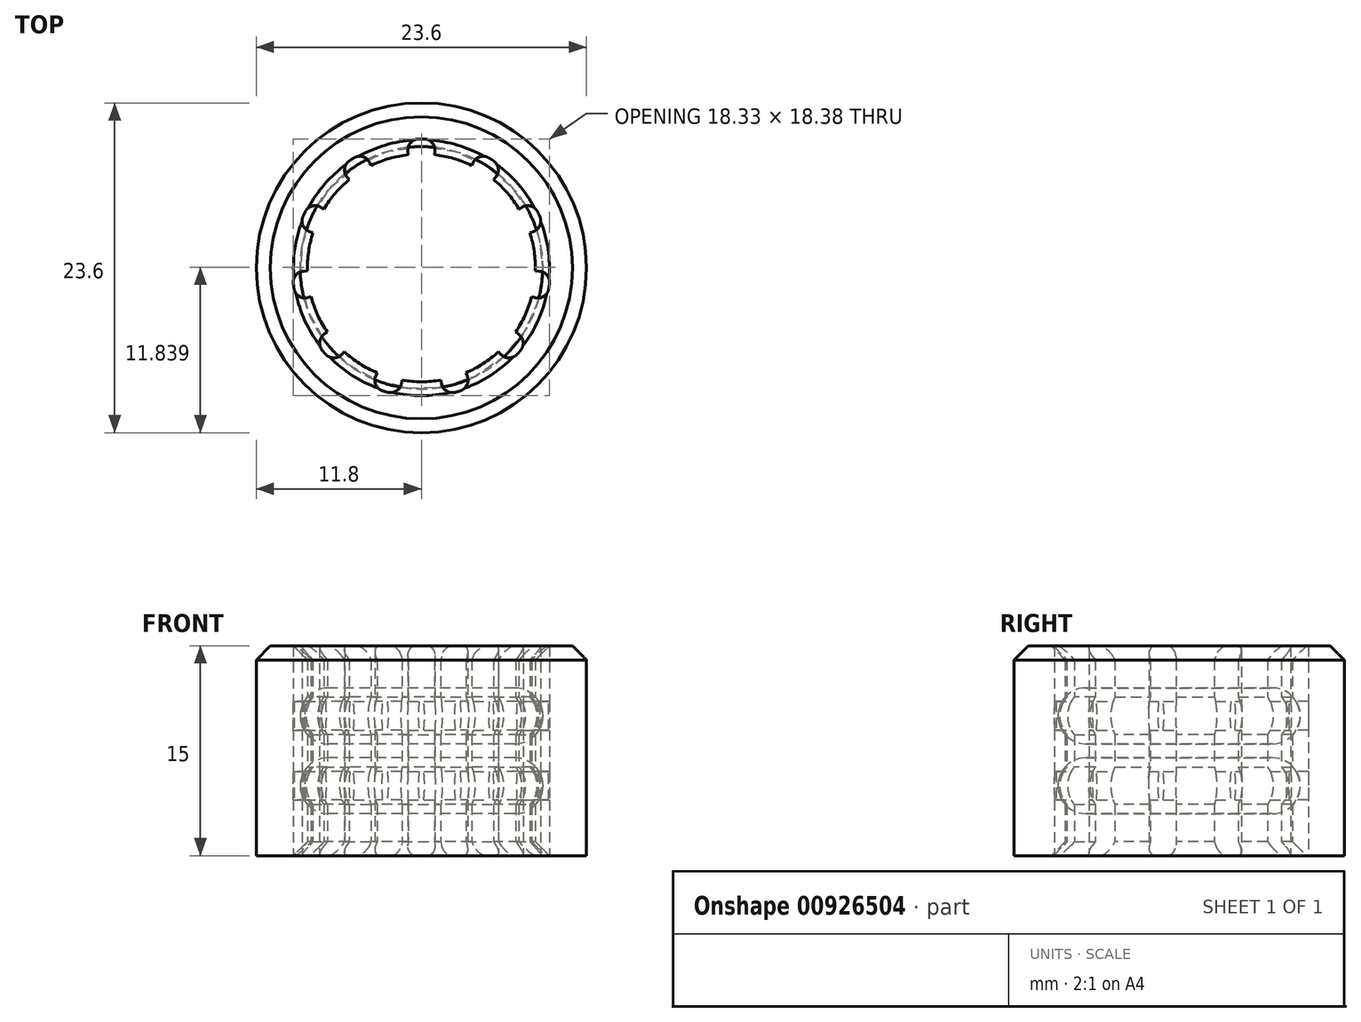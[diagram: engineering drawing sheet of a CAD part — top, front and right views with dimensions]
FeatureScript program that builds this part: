
annotation { "Feature Type Name" : "Feature", "Feature Type Description" : "" }
export const myFeature = defineFeature(function(context is Context, id is Id, definition is map)
    precondition{}
    {
        {
            var Q0;
            Q0=qCreatedBy(makeId("Top.planeOp"),FACE);
            var sketch = newSketch(context, id + "F0", { "sketchPlane" : qUnion([Q0])});
            skArc(sketch, "E0", {"start": v(-0.93, 8.1) * mm, "mid": v(-2.3, 7.82) * mm, "end": v(-3.6, 7.31) * mm});
            skCircle(sketch, "E1", {"center": v(0, 0) * mm, "radius": 11.8 * mm});
            skLineSegment(sketch, "E2", {"start": v(-0.93, 8.1) * mm, "end": v(-1.05, 9.17) * mm});
            skLineSegment(sketch, "E3.MirrorCS", {"start": v(0.93, 8.1) * mm, "end": v(1.05, 9.17) * mm});
            skArc(sketch, "E4", {"start": v(1.05, 9.17) * mm, "mid": v(0, 9.23) * mm, "end": v(-1.05, 9.17) * mm});
            skLineSegment(sketch, "E5.1.0", {"start": v(-5.16, 6.3) * mm, "end": v(-5.84, 7.14) * mm});
            skArc(sketch, "E5.1.1", {"start": v(-4.07, 8.28) * mm, "mid": v(-4.99, 7.76) * mm, "end": v(-5.84, 7.14) * mm});
            skLineSegment(sketch, "E5.1.2", {"start": v(-3.6, 7.31) * mm, "end": v(-4.07, 8.28) * mm});
            skLineSegment(sketch, "E5.2.0", {"start": v(-7.75, 2.52) * mm, "end": v(-8.78, 2.85) * mm});
            skArc(sketch, "E5.2.1", {"start": v(-7.9, 4.77) * mm, "mid": v(-8.4, 3.83) * mm, "end": v(-8.78, 2.85) * mm});
            skLineSegment(sketch, "E5.2.2", {"start": v(-6.98, 4.21) * mm, "end": v(-7.9, 4.77) * mm});
            skLineSegment(sketch, "E5.3.0", {"start": v(-7.88, -2.07) * mm, "end": v(-8.92, -2.35) * mm});
            skArc(sketch, "E5.3.1", {"start": v(-9.22, -0.26) * mm, "mid": v(-9.13, -1.31) * mm, "end": v(-8.92, -2.35) * mm});
            skLineSegment(sketch, "E5.3.2", {"start": v(-8.15, -0.23) * mm, "end": v(-9.22, -0.26) * mm});
            skLineSegment(sketch, "E5.4.0", {"start": v(-5.5, -6) * mm, "end": v(-6.24, -6.8) * mm});
            skArc(sketch, "E5.4.1", {"start": v(-7.62, -5.2) * mm, "mid": v(-6.97, -6.04) * mm, "end": v(-6.24, -6.8) * mm});
            skLineSegment(sketch, "E5.4.2", {"start": v(-6.73, -4.6) * mm, "end": v(-7.62, -5.2) * mm});
            skLineSegment(sketch, "E5.5.0", {"start": v(-1.39, -8.03) * mm, "end": v(-1.57, -9.1) * mm});
            skArc(sketch, "E5.5.1", {"start": v(-3.6, -8.5) * mm, "mid": v(-2.6, -8.85) * mm, "end": v(-1.57, -9.1) * mm});
            skLineSegment(sketch, "E5.5.2", {"start": v(-3.17, -7.5) * mm, "end": v(-3.6, -8.5) * mm});
            skLineSegment(sketch, "E5.6.0", {"start": v(3.17, -7.5) * mm, "end": v(3.6, -8.5) * mm});
            skArc(sketch, "E5.6.1", {"start": v(1.57, -9.1) * mm, "mid": v(2.6, -8.85) * mm, "end": v(3.6, -8.5) * mm});
            skLineSegment(sketch, "E5.6.2", {"start": v(1.39, -8.03) * mm, "end": v(1.57, -9.1) * mm});
            skLineSegment(sketch, "E5.7.0", {"start": v(6.73, -4.6) * mm, "end": v(7.62, -5.2) * mm});
            skArc(sketch, "E5.7.1", {"start": v(6.24, -6.8) * mm, "mid": v(6.97, -6.04) * mm, "end": v(7.62, -5.2) * mm});
            skLineSegment(sketch, "E5.7.2", {"start": v(5.5, -6) * mm, "end": v(6.24, -6.8) * mm});
            skLineSegment(sketch, "E5.8.0", {"start": v(8.15, -0.23) * mm, "end": v(9.22, -0.26) * mm});
            skArc(sketch, "E5.8.1", {"start": v(8.92, -2.35) * mm, "mid": v(9.13, -1.31) * mm, "end": v(9.22, -0.26) * mm});
            skLineSegment(sketch, "E5.8.2", {"start": v(7.88, -2.07) * mm, "end": v(8.92, -2.35) * mm});
            skArc(sketch, "E6.trimOffspring", {"start": v(-5.16, 6.3) * mm, "mid": v(-6.16, 5.34) * mm, "end": v(-6.98, 4.21) * mm});
            skArc(sketch, "E7.trimOffspring", {"start": v(-7.75, 2.52) * mm, "mid": v(-8.07, 1.16) * mm, "end": v(-8.15, -0.23) * mm});
            skArc(sketch, "E8.trimOffspring", {"start": v(-7.88, -2.07) * mm, "mid": v(-7.41, -3.39) * mm, "end": v(-6.73, -4.6) * mm});
            skArc(sketch, "E9.trimOffspring", {"start": v(-5.5, -6) * mm, "mid": v(-4.4, -6.86) * mm, "end": v(-3.17, -7.5) * mm});
            skArc(sketch, "E10.trimOffspring", {"start": v(-1.39, -8.03) * mm, "mid": v(0, -8.15) * mm, "end": v(1.39, -8.03) * mm});
            skArc(sketch, "E11.trimOffspring", {"start": v(3.17, -7.5) * mm, "mid": v(4.4, -6.86) * mm, "end": v(5.5, -6) * mm});
            skArc(sketch, "E12.trimOffspring", {"start": v(6.73, -4.6) * mm, "mid": v(8.07, 1.16) * mm, "end": v(5.16, 6.3) * mm});
            skArc(sketch, "E13.trimOffspring", {"start": v(3.6, 7.31) * mm, "mid": v(2.3, 7.82) * mm, "end": v(0.93, 8.1) * mm});
            skLineSegment(sketch, "E14.1.9.0", {"start": v(6.98, 4.21) * mm, "end": v(7.9, 4.77) * mm});
            skArc(sketch, "E14.3.9.0", {"start": v(8.78, 2.85) * mm, "mid": v(8.4, 3.83) * mm, "end": v(7.9, 4.77) * mm});
            skLineSegment(sketch, "E14.7.9.0", {"start": v(7.75, 2.52) * mm, "end": v(8.78, 2.85) * mm});
            skLineSegment(sketch, "E15.1.10.0", {"start": v(3.6, 7.31) * mm, "end": v(4.07, 8.28) * mm});
            skArc(sketch, "E15.3.10.0", {"start": v(5.84, 7.14) * mm, "mid": v(4.99, 7.76) * mm, "end": v(4.07, 8.28) * mm});
            skLineSegment(sketch, "E15.7.10.0", {"start": v(5.16, 6.3) * mm, "end": v(5.84, 7.14) * mm});
            skSolve(sketch);
        }
        {
            var Q0;
            Q0=makeQuery(id+"F0.imprint","IMPRINT",FACE,{"disambiguationData":[TD([[makeQuery(id+"F0.imprint","IMPRINT",EDGE,{"derivedFrom":sQuery(id+"F0.wireOp",EDGE,"E0")}),-1.0]])]});
            extrude(context, id + "F1", {"entities" : qUnion([Q0]), "depth" : 15 * mm, "offsetDistance" : 25 * mm});
        }
        {
            var Q0;
            Q0=makeQuery(id+"F1.opExtrude","CAP_EDGE",EDGE,{"disambiguationData":[OSD([sQuery(id+"F0.wireOp",EDGE,"E13.trimOffspring")])],"isStart":false});
            var Q1;
            {var subQ0=sQuery(id+"F0.wireOp",EDGE,"E12.trimOffspring");Q1=makeQuery(id+"F1.opExtrude","CAP_EDGE",EDGE,{"disambiguationData":[OSD([subQ0]),TDD([makeQuery(id+"F0.imprint","IMPRINT",EDGE,{"disambiguationData":[TD([[makeQuery(id+"F0.imprint","INTERSECT",VERTEX,{"derivedFrom":[subQ0,sQuery(id+"F0.wireOp",EDGE,"E15.7.10.0")]}),1.0]])],"derivedFrom":subQ0})])],"isStart":false});}
            var Q2;
            {var subQ0=sQuery(id+"F0.wireOp",EDGE,"E12.trimOffspring");Q2=makeQuery(id+"F1.opExtrude","CAP_EDGE",EDGE,{"disambiguationData":[OSD([subQ0]),TDD([makeQuery(id+"F0.imprint","IMPRINT",EDGE,{"disambiguationData":[TD([[makeQuery(id+"F0.imprint","INTERSECT",VERTEX,{"derivedFrom":[sQuery(id+"F0.wireOp",EDGE,"E5.8.0"),subQ0]}),-1.0]])],"derivedFrom":subQ0})])],"isStart":false});}
            var Q3;
            {var subQ0=sQuery(id+"F0.wireOp",EDGE,"E12.trimOffspring");Q3=makeQuery(id+"F1.opExtrude","CAP_EDGE",EDGE,{"disambiguationData":[OSD([subQ0]),TDD([makeQuery(id+"F0.imprint","IMPRINT",EDGE,{"disambiguationData":[TD([[makeQuery(id+"F0.imprint","INTERSECT",VERTEX,{"derivedFrom":[sQuery(id+"F0.wireOp",EDGE,"E5.7.0"),subQ0]}),-1.0]])],"derivedFrom":subQ0})])],"isStart":false});}
            var Q4;
            Q4=makeQuery(id+"F1.opExtrude","CAP_EDGE",EDGE,{"disambiguationData":[OSD([sQuery(id+"F0.wireOp",EDGE,"E11.trimOffspring")])],"isStart":false});
            var Q5;
            Q5=makeQuery(id+"F1.opExtrude","CAP_EDGE",EDGE,{"disambiguationData":[OSD([sQuery(id+"F0.wireOp",EDGE,"E10.trimOffspring")])],"isStart":false});
            var Q6;
            Q6=makeQuery(id+"F1.opExtrude","CAP_EDGE",EDGE,{"disambiguationData":[OSD([sQuery(id+"F0.wireOp",EDGE,"E9.trimOffspring")])],"isStart":false});
            var Q7;
            Q7=makeQuery(id+"F1.opExtrude","CAP_EDGE",EDGE,{"disambiguationData":[OSD([sQuery(id+"F0.wireOp",EDGE,"E8.trimOffspring")])],"isStart":false});
            var Q8;
            Q8=makeQuery(id+"F1.opExtrude","CAP_EDGE",EDGE,{"disambiguationData":[OSD([sQuery(id+"F0.wireOp",EDGE,"E7.trimOffspring")])],"isStart":false});
            var Q9;
            Q9=makeQuery(id+"F1.opExtrude","CAP_EDGE",EDGE,{"disambiguationData":[OSD([sQuery(id+"F0.wireOp",EDGE,"E6.trimOffspring")])],"isStart":false});
            var Q10;
            Q10=makeQuery(id+"F1.opExtrude","CAP_EDGE",EDGE,{"disambiguationData":[OSD([sQuery(id+"F0.wireOp",EDGE,"E0")])],"isStart":false});
            var Q11;
            Q11=makeQuery(id+"F1.opExtrude","CAP_EDGE",EDGE,{"disambiguationData":[OSD([sQuery(id+"F0.wireOp",EDGE,"E6.trimOffspring")])],"isStart":true});
            var Q12;
            Q12=makeQuery(id+"F1.opExtrude","CAP_EDGE",EDGE,{"disambiguationData":[OSD([sQuery(id+"F0.wireOp",EDGE,"E7.trimOffspring")])],"isStart":true});
            var Q13;
            Q13=makeQuery(id+"F1.opExtrude","CAP_EDGE",EDGE,{"disambiguationData":[OSD([sQuery(id+"F0.wireOp",EDGE,"E8.trimOffspring")])],"isStart":true});
            var Q14;
            Q14=makeQuery(id+"F1.opExtrude","CAP_EDGE",EDGE,{"disambiguationData":[OSD([sQuery(id+"F0.wireOp",EDGE,"E9.trimOffspring")])],"isStart":true});
            var Q15;
            Q15=makeQuery(id+"F1.opExtrude","CAP_EDGE",EDGE,{"disambiguationData":[OSD([sQuery(id+"F0.wireOp",EDGE,"E10.trimOffspring")])],"isStart":true});
            var Q16;
            Q16=makeQuery(id+"F1.opExtrude","CAP_EDGE",EDGE,{"disambiguationData":[OSD([sQuery(id+"F0.wireOp",EDGE,"E11.trimOffspring")])],"isStart":true});
            var Q17;
            {var subQ0=sQuery(id+"F0.wireOp",EDGE,"E12.trimOffspring");Q17=makeQuery(id+"F1.opExtrude","CAP_EDGE",EDGE,{"disambiguationData":[OSD([subQ0]),TDD([makeQuery(id+"F0.imprint","IMPRINT",EDGE,{"disambiguationData":[TD([[makeQuery(id+"F0.imprint","INTERSECT",VERTEX,{"derivedFrom":[sQuery(id+"F0.wireOp",EDGE,"E5.7.0"),subQ0]}),-1.0]])],"derivedFrom":subQ0})])],"isStart":true});}
            var Q18;
            {var subQ0=sQuery(id+"F0.wireOp",EDGE,"E12.trimOffspring");Q18=makeQuery(id+"F1.opExtrude","CAP_EDGE",EDGE,{"disambiguationData":[OSD([subQ0]),TDD([makeQuery(id+"F0.imprint","IMPRINT",EDGE,{"disambiguationData":[TD([[makeQuery(id+"F0.imprint","INTERSECT",VERTEX,{"derivedFrom":[sQuery(id+"F0.wireOp",EDGE,"E5.8.0"),subQ0]}),-1.0]])],"derivedFrom":subQ0})])],"isStart":true});}
            var Q19;
            {var subQ0=sQuery(id+"F0.wireOp",EDGE,"E12.trimOffspring");Q19=makeQuery(id+"F1.opExtrude","CAP_EDGE",EDGE,{"disambiguationData":[OSD([subQ0]),TDD([makeQuery(id+"F0.imprint","IMPRINT",EDGE,{"disambiguationData":[TD([[makeQuery(id+"F0.imprint","INTERSECT",VERTEX,{"derivedFrom":[subQ0,sQuery(id+"F0.wireOp",EDGE,"E15.7.10.0")]}),1.0]])],"derivedFrom":subQ0})])],"isStart":true});}
            var Q20;
            Q20=makeQuery(id+"F1.opExtrude","CAP_EDGE",EDGE,{"disambiguationData":[OSD([sQuery(id+"F0.wireOp",EDGE,"E13.trimOffspring")])],"isStart":true});
            var Q21;
            Q21=makeQuery(id+"F1.opExtrude","CAP_EDGE",EDGE,{"disambiguationData":[OSD([sQuery(id+"F0.wireOp",EDGE,"E0")])],"isStart":true});
            chamfer(context, id + "F2", {"entities" : qUnion([Q0, Q1, Q2, Q3, Q4, Q5, Q6, Q7, Q8, Q9, Q10, Q11, Q12, Q13, Q14, Q15, Q16, Q17, Q18, Q19, Q20, Q21]), "width" : 1 * mm, "tangentPropagation" : true});
        }
        {
            var Q0;
            Q0=qCreatedBy(makeId("Top.planeOp"),FACE);
            cPlane(context, id + "F3", {"entities" : qUnion([Q0]), "cplaneType" : CPlaneType.OFFSET, "offset" : 5 * mm, "width" : 150 * mm, "height" : 150 * mm});
        }
        {
            var Q0;
            Q0=qCreatedBy(id+"F3.planeOp",FACE);
            var sketch = newSketch(context, id + "F4", { "sketchPlane" : qUnion([Q0])});
            skCircle(sketch, "E16", {"center": v(0, 0) * mm, "radius": 8.67 * mm});
            skSolve(sketch);
        }
        {
            var Q0;
            Q0=makeQuery(id+"F4.imprint","IMPRINT",FACE,{"disambiguationData":[TD([[makeQuery(id+"F4.imprint","IMPRINT",EDGE,{"derivedFrom":sQuery(id+"F4.wireOp",EDGE,"E16")}),1.0]])]});
            extrude(context, id + "F5", {"entities" : qUnion([Q0]), "depth" : 2 * mm, "offsetDistance" : 25 * mm, "hasSecondDirection" : true, "secondDirectionOppositeDirection" : true, "secondDirectionDepth" : 2 * mm});
        }
        {
            var Q0;
            Q0=makeQuery(id+"F5.opExtrude","SWEPT_FACE",FACE,{"disambiguationData":[OSD([sQuery(id+"F4.wireOp",EDGE,"E16")])]});
            fillet(context, id + "F6", {"entities" : qUnion([Q0]), "radius" : 2 * mm, "tangentPropagation" : true, "allowEdgeOverflow" : false});
        }
        {
            var Q0;
            Q0=makeQuery(id+"F5.opExtrude","SWEPT_BODY",BODY,{"disambiguationData":[OSD([sQuery(id+"F4.wireOp",EDGE,"E16")])]});
            var Q1;
            Q1=makeQuery(id+"F1.opExtrude","SWEPT_BODY",BODY,{"disambiguationData":[OSD([sQuery(id+"F0.wireOp",EDGE,"E0"),sQuery(id+"F0.wireOp",EDGE,"E1"),sQuery(id+"F0.wireOp",EDGE,"E2"),sQuery(id+"F0.wireOp",EDGE,"E3.MirrorCS"),sQuery(id+"F0.wireOp",EDGE,"E4"),sQuery(id+"F0.wireOp",EDGE,"E5.1.0"),sQuery(id+"F0.wireOp",EDGE,"E5.1.1"),sQuery(id+"F0.wireOp",EDGE,"E5.1.2"),sQuery(id+"F0.wireOp",EDGE,"E5.2.0"),sQuery(id+"F0.wireOp",EDGE,"E5.2.1"),sQuery(id+"F0.wireOp",EDGE,"E5.2.2"),sQuery(id+"F0.wireOp",EDGE,"E5.3.0"),sQuery(id+"F0.wireOp",EDGE,"E5.3.1"),sQuery(id+"F0.wireOp",EDGE,"E5.3.2"),sQuery(id+"F0.wireOp",EDGE,"E5.4.0"),sQuery(id+"F0.wireOp",EDGE,"E5.4.1"),sQuery(id+"F0.wireOp",EDGE,"E5.4.2"),sQuery(id+"F0.wireOp",EDGE,"E5.5.0"),sQuery(id+"F0.wireOp",EDGE,"E5.5.1"),sQuery(id+"F0.wireOp",EDGE,"E5.5.2"),sQuery(id+"F0.wireOp",EDGE,"E5.6.0"),sQuery(id+"F0.wireOp",EDGE,"E5.6.1"),sQuery(id+"F0.wireOp",EDGE,"E5.6.2"),sQuery(id+"F0.wireOp",EDGE,"E5.7.0"),sQuery(id+"F0.wireOp",EDGE,"E5.7.1"),sQuery(id+"F0.wireOp",EDGE,"E5.7.2"),sQuery(id+"F0.wireOp",EDGE,"E5.8.0"),sQuery(id+"F0.wireOp",EDGE,"E5.8.1"),sQuery(id+"F0.wireOp",EDGE,"E5.8.2"),sQuery(id+"F0.wireOp",EDGE,"E6.trimOffspring"),sQuery(id+"F0.wireOp",EDGE,"E7.trimOffspring"),sQuery(id+"F0.wireOp",EDGE,"E8.trimOffspring"),sQuery(id+"F0.wireOp",EDGE,"E9.trimOffspring"),sQuery(id+"F0.wireOp",EDGE,"E10.trimOffspring"),sQuery(id+"F0.wireOp",EDGE,"E11.trimOffspring"),sQuery(id+"F0.wireOp",EDGE,"E12.trimOffspring"),sQuery(id+"F0.wireOp",EDGE,"E13.trimOffspring"),sQuery(id+"F0.wireOp",EDGE,"E14.1.9.0"),sQuery(id+"F0.wireOp",EDGE,"E14.3.9.0"),sQuery(id+"F0.wireOp",EDGE,"E14.7.9.0"),sQuery(id+"F0.wireOp",EDGE,"E15.1.10.0"),sQuery(id+"F0.wireOp",EDGE,"E15.3.10.0"),sQuery(id+"F0.wireOp",EDGE,"E15.7.10.0")])]});
            booleanBodies(context, id + "F7", {"operationType" : BooleanOperationType.SUBTRACTION, "tools" : qUnion([Q0]), "targets" : qUnion([Q1]), "keepTools" : true});
        }
        {
            var Q0;
            Q0=makeQuery(id+"F1.opExtrude","CAP_EDGE",EDGE,{"disambiguationData":[OSD([sQuery(id+"F0.wireOp",EDGE,"E1")])],"isStart":false});
            chamfer(context, id + "F8", {"entities" : qUnion([Q0]), "width" : 1 * mm, "tangentPropagation" : true});
        }
        {
            var Q0;
            Q0=makeQuery(id+"F5.opExtrude","SWEPT_BODY",BODY,{"disambiguationData":[OSD([sQuery(id+"F4.wireOp",EDGE,"E16")])]});
            transform(context, id + "F9", {"entities" : qUnion([Q0]), "transformType" : TransformType.TRANSLATION_3D, "dx" : 0 * mm, "dy" : 0 * mm, "dz" : 5 * mm, "makeCopy" : true});
        }
        {
            var Q0;
            Q0=makeQuery(id+"F9.opPattern","COPY",BODY,{"derivedFrom":makeQuery(id+"F5.opExtrude","SWEPT_BODY",BODY,{"disambiguationData":[OSD([sQuery(id+"F4.wireOp",EDGE,"E16")])]}),"instanceName":"1"});
            var Q1;
            Q1=makeQuery(id+"F1.opExtrude","SWEPT_BODY",BODY,{"disambiguationData":[OSD([sQuery(id+"F0.wireOp",EDGE,"E0"),sQuery(id+"F0.wireOp",EDGE,"E1"),sQuery(id+"F0.wireOp",EDGE,"E2"),sQuery(id+"F0.wireOp",EDGE,"E3.MirrorCS"),sQuery(id+"F0.wireOp",EDGE,"E4"),sQuery(id+"F0.wireOp",EDGE,"E5.1.0"),sQuery(id+"F0.wireOp",EDGE,"E5.1.1"),sQuery(id+"F0.wireOp",EDGE,"E5.1.2"),sQuery(id+"F0.wireOp",EDGE,"E5.2.0"),sQuery(id+"F0.wireOp",EDGE,"E5.2.1"),sQuery(id+"F0.wireOp",EDGE,"E5.2.2"),sQuery(id+"F0.wireOp",EDGE,"E5.3.0"),sQuery(id+"F0.wireOp",EDGE,"E5.3.1"),sQuery(id+"F0.wireOp",EDGE,"E5.3.2"),sQuery(id+"F0.wireOp",EDGE,"E5.4.0"),sQuery(id+"F0.wireOp",EDGE,"E5.4.1"),sQuery(id+"F0.wireOp",EDGE,"E5.4.2"),sQuery(id+"F0.wireOp",EDGE,"E5.5.0"),sQuery(id+"F0.wireOp",EDGE,"E5.5.1"),sQuery(id+"F0.wireOp",EDGE,"E5.5.2"),sQuery(id+"F0.wireOp",EDGE,"E5.6.0"),sQuery(id+"F0.wireOp",EDGE,"E5.6.1"),sQuery(id+"F0.wireOp",EDGE,"E5.6.2"),sQuery(id+"F0.wireOp",EDGE,"E5.7.0"),sQuery(id+"F0.wireOp",EDGE,"E5.7.1"),sQuery(id+"F0.wireOp",EDGE,"E5.7.2"),sQuery(id+"F0.wireOp",EDGE,"E5.8.0"),sQuery(id+"F0.wireOp",EDGE,"E5.8.1"),sQuery(id+"F0.wireOp",EDGE,"E5.8.2"),sQuery(id+"F0.wireOp",EDGE,"E6.trimOffspring"),sQuery(id+"F0.wireOp",EDGE,"E7.trimOffspring"),sQuery(id+"F0.wireOp",EDGE,"E8.trimOffspring"),sQuery(id+"F0.wireOp",EDGE,"E9.trimOffspring"),sQuery(id+"F0.wireOp",EDGE,"E10.trimOffspring"),sQuery(id+"F0.wireOp",EDGE,"E11.trimOffspring"),sQuery(id+"F0.wireOp",EDGE,"E12.trimOffspring"),sQuery(id+"F0.wireOp",EDGE,"E13.trimOffspring"),sQuery(id+"F0.wireOp",EDGE,"E14.1.9.0"),sQuery(id+"F0.wireOp",EDGE,"E14.3.9.0"),sQuery(id+"F0.wireOp",EDGE,"E14.7.9.0"),sQuery(id+"F0.wireOp",EDGE,"E15.1.10.0"),sQuery(id+"F0.wireOp",EDGE,"E15.3.10.0"),sQuery(id+"F0.wireOp",EDGE,"E15.7.10.0")])]});
            booleanBodies(context, id + "F10", {"operationType" : BooleanOperationType.SUBTRACTION, "tools" : qUnion([Q0]), "targets" : qUnion([Q1]), "keepTools" : true});
        }
        {
            var Q0;
            Q0=makeQuery(id+"F1.opExtrude","SWEPT_EDGE",EDGE,{"disambiguationData":[OSD([sQuery(id+"F0.wireOp",EDGE,"E5.1.1"),sQuery(id+"F0.wireOp",EDGE,"E5.1.2")])]});
            var Q1;
            Q1=makeQuery(id+"F1.opExtrude","SWEPT_EDGE",EDGE,{"disambiguationData":[OSD([sQuery(id+"F0.wireOp",EDGE,"E2"),sQuery(id+"F0.wireOp",EDGE,"E4")])]});
            var Q2;
            Q2=makeQuery(id+"F1.opExtrude","SWEPT_EDGE",EDGE,{"disambiguationData":[OSD([sQuery(id+"F0.wireOp",EDGE,"E15.1.10.0"),sQuery(id+"F0.wireOp",EDGE,"E15.3.10.0")])]});
            var Q3;
            Q3=makeQuery(id+"F1.opExtrude","SWEPT_EDGE",EDGE,{"disambiguationData":[OSD([sQuery(id+"F0.wireOp",EDGE,"E3.MirrorCS"),sQuery(id+"F0.wireOp",EDGE,"E4")])]});
            var Q4;
            Q4=makeQuery(id+"F1.opExtrude","SWEPT_EDGE",EDGE,{"disambiguationData":[OSD([sQuery(id+"F0.wireOp",EDGE,"E15.3.10.0"),sQuery(id+"F0.wireOp",EDGE,"E15.7.10.0")])]});
            var Q5;
            Q5=makeQuery(id+"F1.opExtrude","SWEPT_EDGE",EDGE,{"disambiguationData":[OSD([sQuery(id+"F0.wireOp",EDGE,"E14.1.9.0"),sQuery(id+"F0.wireOp",EDGE,"E14.3.9.0")])]});
            var Q6;
            Q6=makeQuery(id+"F1.opExtrude","SWEPT_EDGE",EDGE,{"disambiguationData":[OSD([sQuery(id+"F0.wireOp",EDGE,"E5.8.0"),sQuery(id+"F0.wireOp",EDGE,"E5.8.1")])]});
            var Q7;
            Q7=makeQuery(id+"F1.opExtrude","SWEPT_EDGE",EDGE,{"disambiguationData":[OSD([sQuery(id+"F0.wireOp",EDGE,"E5.7.0"),sQuery(id+"F0.wireOp",EDGE,"E5.7.1")])]});
            var Q8;
            Q8=makeQuery(id+"F1.opExtrude","SWEPT_EDGE",EDGE,{"disambiguationData":[OSD([sQuery(id+"F0.wireOp",EDGE,"E14.3.9.0"),sQuery(id+"F0.wireOp",EDGE,"E14.7.9.0")])]});
            var Q9;
            Q9=makeQuery(id+"F1.opExtrude","SWEPT_EDGE",EDGE,{"disambiguationData":[OSD([sQuery(id+"F0.wireOp",EDGE,"E5.8.1"),sQuery(id+"F0.wireOp",EDGE,"E5.8.2")])]});
            var Q10;
            Q10=makeQuery(id+"F1.opExtrude","SWEPT_EDGE",EDGE,{"disambiguationData":[OSD([sQuery(id+"F0.wireOp",EDGE,"E5.7.1"),sQuery(id+"F0.wireOp",EDGE,"E5.7.2")])]});
            var Q11;
            Q11=makeQuery(id+"F1.opExtrude","SWEPT_EDGE",EDGE,{"disambiguationData":[OSD([sQuery(id+"F0.wireOp",EDGE,"E5.6.0"),sQuery(id+"F0.wireOp",EDGE,"E5.6.1")])]});
            var Q12;
            Q12=makeQuery(id+"F1.opExtrude","SWEPT_EDGE",EDGE,{"disambiguationData":[OSD([sQuery(id+"F0.wireOp",EDGE,"E5.6.1"),sQuery(id+"F0.wireOp",EDGE,"E5.6.2")])]});
            var Q13;
            Q13=makeQuery(id+"F1.opExtrude","SWEPT_EDGE",EDGE,{"disambiguationData":[OSD([sQuery(id+"F0.wireOp",EDGE,"E5.5.0"),sQuery(id+"F0.wireOp",EDGE,"E5.5.1")])]});
            var Q14;
            Q14=makeQuery(id+"F1.opExtrude","SWEPT_EDGE",EDGE,{"disambiguationData":[OSD([sQuery(id+"F0.wireOp",EDGE,"E5.5.1"),sQuery(id+"F0.wireOp",EDGE,"E5.5.2")])]});
            var Q15;
            Q15=makeQuery(id+"F1.opExtrude","SWEPT_EDGE",EDGE,{"disambiguationData":[OSD([sQuery(id+"F0.wireOp",EDGE,"E5.2.0"),sQuery(id+"F0.wireOp",EDGE,"E5.2.1")])]});
            var Q16;
            Q16=makeQuery(id+"F1.opExtrude","SWEPT_EDGE",EDGE,{"disambiguationData":[OSD([sQuery(id+"F0.wireOp",EDGE,"E5.3.0"),sQuery(id+"F0.wireOp",EDGE,"E5.3.1")])]});
            var Q17;
            Q17=makeQuery(id+"F1.opExtrude","SWEPT_EDGE",EDGE,{"disambiguationData":[OSD([sQuery(id+"F0.wireOp",EDGE,"E5.4.1"),sQuery(id+"F0.wireOp",EDGE,"E5.4.2")])]});
            var Q18;
            Q18=makeQuery(id+"F1.opExtrude","SWEPT_EDGE",EDGE,{"disambiguationData":[OSD([sQuery(id+"F0.wireOp",EDGE,"E5.3.1"),sQuery(id+"F0.wireOp",EDGE,"E5.3.2")])]});
            var Q19;
            Q19=makeQuery(id+"F1.opExtrude","SWEPT_EDGE",EDGE,{"disambiguationData":[OSD([sQuery(id+"F0.wireOp",EDGE,"E5.4.0"),sQuery(id+"F0.wireOp",EDGE,"E5.4.1")])]});
            var Q20;
            Q20=makeQuery(id+"F1.opExtrude","SWEPT_EDGE",EDGE,{"disambiguationData":[OSD([sQuery(id+"F0.wireOp",EDGE,"E5.2.1"),sQuery(id+"F0.wireOp",EDGE,"E5.2.2")])]});
            var Q21;
            Q21=makeQuery(id+"F1.opExtrude","SWEPT_EDGE",EDGE,{"disambiguationData":[OSD([sQuery(id+"F0.wireOp",EDGE,"E5.1.0"),sQuery(id+"F0.wireOp",EDGE,"E5.1.1")])]});
            fillet(context, id + "F11", {"entities" : qUnion([Q0, Q1, Q2, Q3, Q4, Q5, Q6, Q7, Q8, Q9, Q10, Q11, Q12, Q13, Q14, Q15, Q16, Q17, Q18, Q19, Q20, Q21]), "radius" : 0.8 * mm, "tangentPropagation" : true, "allowEdgeOverflow" : false});
        }
    });
